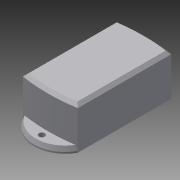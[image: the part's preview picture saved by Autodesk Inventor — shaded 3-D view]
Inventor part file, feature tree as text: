
AUTODESK INVENTOR PART (.ipt)
format: ipt  version: 2013 SP2 (Build 170200200, 200)  size: 123,904 bytes
history: native  units: mm
features: sketch x3, extrude x2, chamfer x2, hole x1
ambient origin geometry x8: Origin, YZ Plane, XZ Plane, XY Plane, X Axis, Y Axis, Z Axis, Center Point
bodies: Solid1 (feature_tree)
feature tree (8):
  extrude  "Extrusion1"  Depth=31.5mm
  extrude  "Extrusion2"  Depth=28.0mm TaperAngle=0.0deg
  chamfer  "Chamfer1"  Distance=4.0mm
  chamfer  "Chamfer2"  Distance=2.0mm Angle=45.0deg
  hole  "Hole1"  [1 undecoded]
  sketch  "Sketch1"  dims[d5=37.0mm d6=31.5mm]
  sketch  "Sketch2"  dims[d7=1.5mm d8=28.0mm d9=0.0mm]
  sketch  "Sketch3"  dims[d10=75.5mm d11=4.0mm d12=0.0mm d13=2.0mm d14=2.0mm d15=45.0deg d16=3.0mm d17=2.0mm d18=3.490659mm d19=4.0mm d20=6.0mm d21=4.0mm d22=2.0mm d23=90.0deg d24=8.0mm d25=0.0mm]
note: 1 required parameter value undecoded (feature->parameter linkage not recoverable at this tier; creation-order binding heuristic only, values carry confidence <= 0.55)
